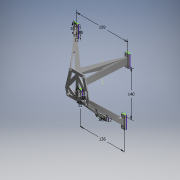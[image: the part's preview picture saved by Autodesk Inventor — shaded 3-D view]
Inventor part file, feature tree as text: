
AUTODESK INVENTOR PART (.ipt)
format: ipt  version: 2019 (Build 230136000, 136)  size: 622,592 bytes
history: native  units: mm (DEFAULTED — no unit token found)
features: other x19, extrude x15, loft x9, sketch x6, hole x2, chamfer x2, projected_geometry x1
ambient origin geometry x8: Origin, YZ Plane, XZ Plane, XY Plane, X Axis, Y Axis, Z Axis, Center Point
bodies: Solid1 (feature_tree)
feature tree (54):
  sketch  "Sketch1"  dims[d0=40.0mm d1=42.0mm]
  extrude  "Extrusion1"  Depth=42.0mm
  extrude  "Extrusion2"  Depth=56.0mm
  other  "deck_plate"
  sketch  "Sketch2"  dims[d2=28.0mm d3=56.0mm]
  extrude  "Extrusion3"  Depth=3.0mm
  extrude  "Extrusion4"  Depth=3.0mm
  extrude  "Extrusion5"  Depth=74.0mm
  loft  "Loft1"
  extrude  "Extrusion6"  Depth=8.0mm
  extrude  "Extrusion7"  Depth=9.0mm
  loft  "Loft2"
  loft  "Loft3"
  extrude  "Extrusion8"  Depth=8.0mm
  loft  "Loft4"
  loft  "Loft5"
  extrude  "Extrusion9"  Depth=8.5mm
  extrude  "Extrusion10"  Depth=8.5mm
  extrude  "Extrusion11"  Depth=20.0mm
  loft  "Loft6"
  loft  "Loft7"
  extrude  "Extrusion12"  Depth=10.0mm
  loft  "Loft8"
  loft  "Loft9"
  hole  "Hole1"  [1 undecoded]
  hole  "Hole2"  [1 undecoded]
  extrude  "Extrusion13"  Depth=8.5mm
  sketch  "Sketch6"  dims[d11=63.0mm d12=2.5mm d13=8.0mm d14=9.0mm d15=4.0mm d16=8.0mm d17=8.0mm d18=12.0mm d19=8.5mm d20=8.5mm d21=8.5mm d26=20.0mm d27=5.0mm d30=5.0mm d31=10.0mm d32=5.0mm d33=15.0mm d35=10.0mm d36=5.0mm d37=0.0mm d38=8.5mm d39=23.5mm d40=10.0mm d41=5.0mm d42=2.0mm d43=0.0mm d44=-75.0mm d45=3.0mm d46=27.0mm d47=37.5mm d48=20.0mm d49=5.0mm d50=12.0mm d51=3.5mm d52=0.0mm d53=3.6mm d54=0.0mm d55=0.1mm d56=0.0mm d57=0.0mm d58=90.0deg d59=0.0mm d60=90.0deg d61=3.0mm d62=3.0mm d63=30.0mm d64=12.0mm d65=40.0mm d66=5.0mm d67=20.0mm d68=136.0mm d69=4.5mm d70=3.5mm d71=0.0mm d72=3.6mm d73=0.0mm d74=0.0mm d75=90.0deg d76=0.0mm d77=90.0deg d78=0.0mm d79=90.0deg d80=0.0mm d81=90.0deg d82=0.1mm d83=0.0mm d84=0.0mm d85=90.0deg d86=0.0mm d87=90.0deg d88=0.0mm d89=90.0deg d90=0.0mm d91=90.0deg d92=3.0mm d93=3.0mm d94=30.0mm d95=12.0mm d96=40.0mm d97=5.0mm d98=20.0mm d99=159.0mm d100=140.0mm d101=5.0mm d102=15.0mm d103=10.0mm d104=0.1mm d105=0.0mm d106=3.5mm d107=0.0mm d108=3.6mm d109=0.0mm d110=0.0mm d111=90.0deg d112=0.0mm d113=90.0deg d114=0.0mm d115=90.0deg d116=0.0mm d117=90.0deg d118=5.0mm d119=20.0mm d120=10.0mm d121=0.1mm d122=0.0mm d123=0.0mm d124=90.0deg d125=0.0mm d126=90.0deg d127=0.0mm d128=90.0deg d129=0.0mm d130=90.0deg d131=6.0mm d132=6.0mm d133=4.0mm d134=2.0mm d135=90.0deg d136=8.0mm d137=20.594885mm d138=3.2mm d139=6.0mm d140=4.0mm d141=2.0mm d142=90.0deg d143=8.0mm d144=20.594885mm d148=1.0mm d149=0.0mm d150=21.0mm d151=6.0mm d152=3.0mm d153=3.0mm d154=3.0mm d155=3.0mm d156=4.25mm d157=0.0mm d158=3.0mm d159=0.0mm d160=1.75mm d161=4.0mm d162=45.0deg d163=23.0mm d164=4.0mm d165=45.0deg]
  extrude  "Extrusion14"  Depth=23.5mm
  extrude  "Extrusion15"  Depth=10.0mm
  chamfer  "Chamfer1"  Distance=5.0mm
  chamfer  "Chamfer2"  Distance=2.0mm
  other  "Edges1"
  other  "Edges2"
  other  "Edges3"
  other  "Edges4"
  other  "Edges5"
  other  "Edges6"
  other  "Edges7"
  other  "Edges8"
  other  "Edges9"
  other  "Edges10"
  other  "Edges11"
  other  "Edges12"
  other  "Edges13"
  other  "Edges14"
  other  "Edges15"
  other  "Edges16"
  other  "Edges17"
  other  "Edges18"
  sketch  "Sketch3"  dims[d5=3.0mm d6=3.0mm]
  sketch  "Sketch4"  dims[d7=3.0mm d8=3.0mm]
  sketch  "Sketch5"  dims[d9=45.0mm d10=74.0mm]
  projected_geometry  "Projected Loop1"
note: 2 required parameter values undecoded (feature->parameter linkage not recoverable at this tier; creation-order binding heuristic only, values carry confidence <= 0.55)
